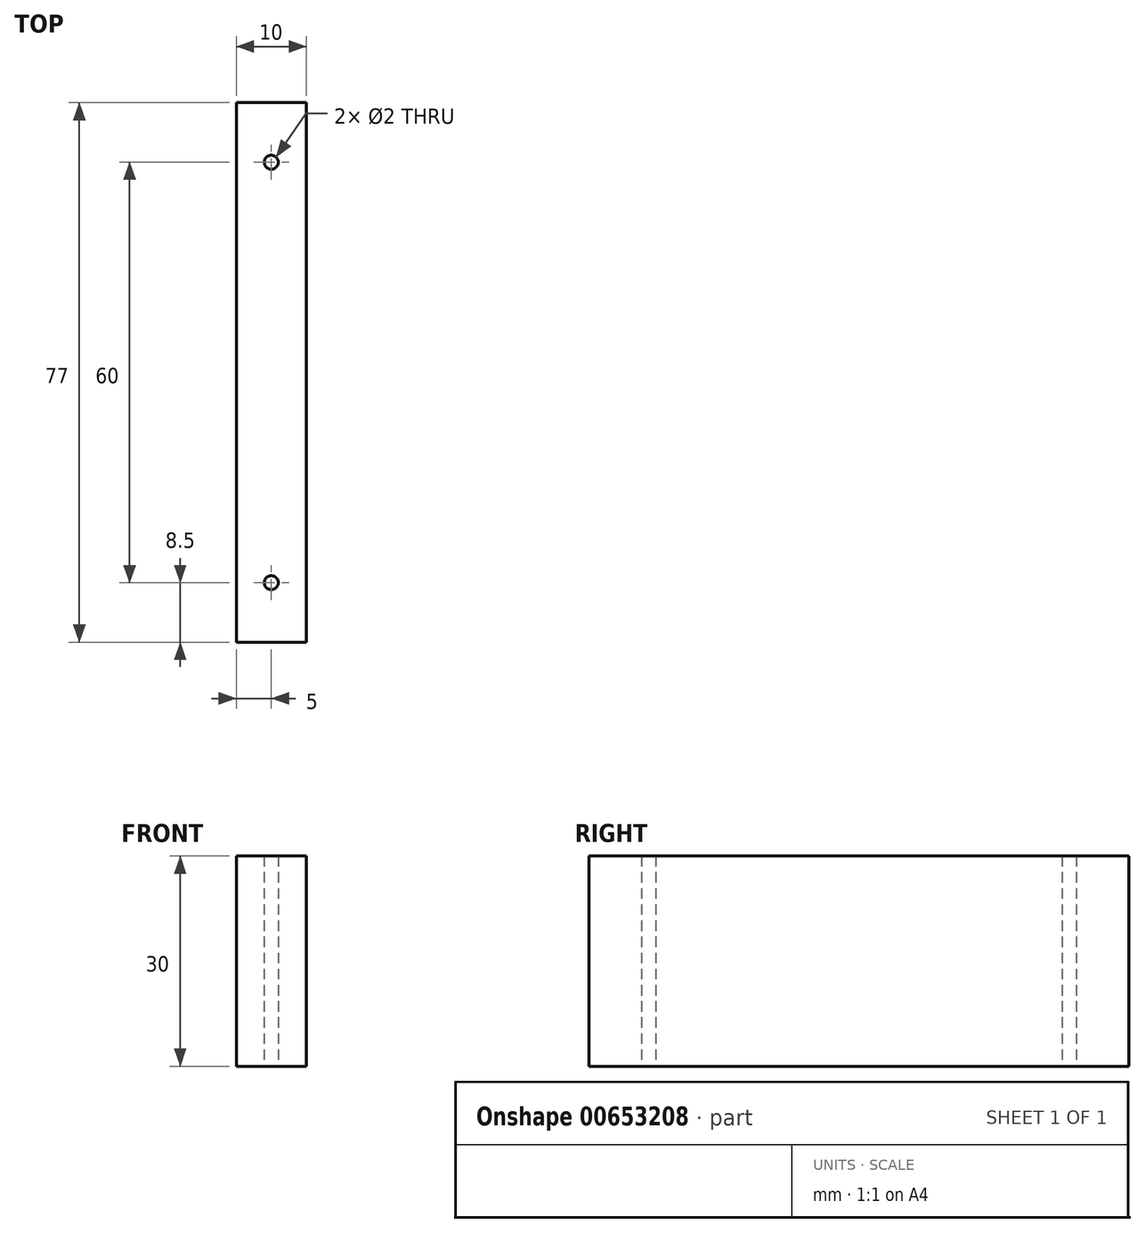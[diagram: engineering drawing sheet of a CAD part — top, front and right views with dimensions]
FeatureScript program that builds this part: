
annotation { "Feature Type Name" : "Feature", "Feature Type Description" : "" }
export const myFeature = defineFeature(function(context is Context, id is Id, definition is map)
    precondition{}
    {
        {
            var Q0;
            Q0=qCreatedBy(makeId("Front.planeOp"),FACE);
            var sketch = newSketch(context, id + "F0", { "sketchPlane" : qUnion([Q0])});
            skLineSegment(sketch, "E0.bottom", {"start": v(0, 0) * mm, "end": v(10, 0) * mm});
            skLineSegment(sketch, "E0.top", {"start": v(0, 30) * mm, "end": v(10, 30) * mm});
            skLineSegment(sketch, "E0.left", {"start": v(0, 0) * mm, "end": v(0, 30) * mm});
            skLineSegment(sketch, "E0.right", {"start": v(10, 0) * mm, "end": v(10, 30) * mm});
            skSolve(sketch);
        }
        {
            var Q0;
            Q0 = qSketchRegion(id + "F0", true);
            extrude(context, id + "F1", {"entities" : qUnion([Q0]), "depth" : 77 * mm, "offsetDistance" : 25 * mm});
        }
        {
            var Q0;
            Q0=makeQuery(id+"F1.opExtrude","SWEPT_FACE",FACE,{"disambiguationData":[OSD([sQuery(id+"F0.wireOp",EDGE,"E0.bottom")])]});
            var sketch = newSketch(context, id + "F2", { "sketchPlane" : qUnion([Q0])});
            skLineSegment(sketch, "E1", {"start": v(5, 90.93) * mm, "end": v(5, -8.75) * mm, "construction": true});
            skPoint(sketch, "E1.startSnap0", {"position": v(5, 77) * mm});
            skLineSegment(sketch, "E2", {"start": v(-10.1, 38.5) * mm, "end": v(20.73, 38.5) * mm, "construction": true});
            skPoint(sketch, "E2.startSnap0", {"position": v(0, 38.5) * mm});
            skCircle(sketch, "E3", {"center": v(5, 68.5) * mm, "radius": 1 * mm});
            skCircle(sketch, "E4", {"center": v(5, 8.5) * mm, "radius": 1 * mm});
            skSolve(sketch);
        }
        {
            var Q0;
            Q0 = qSketchRegion(id + "F2", true);
            extrude(context, id + "F3", {"entities" : qUnion([Q0]), "operationType" : NewBodyOperationType.REMOVE, "endBound" : BoundingType.THROUGH_ALL, "oppositeDirection" : true, "depth" : 25 * mm, "offsetDistance" : 25 * mm});
        }
    });
